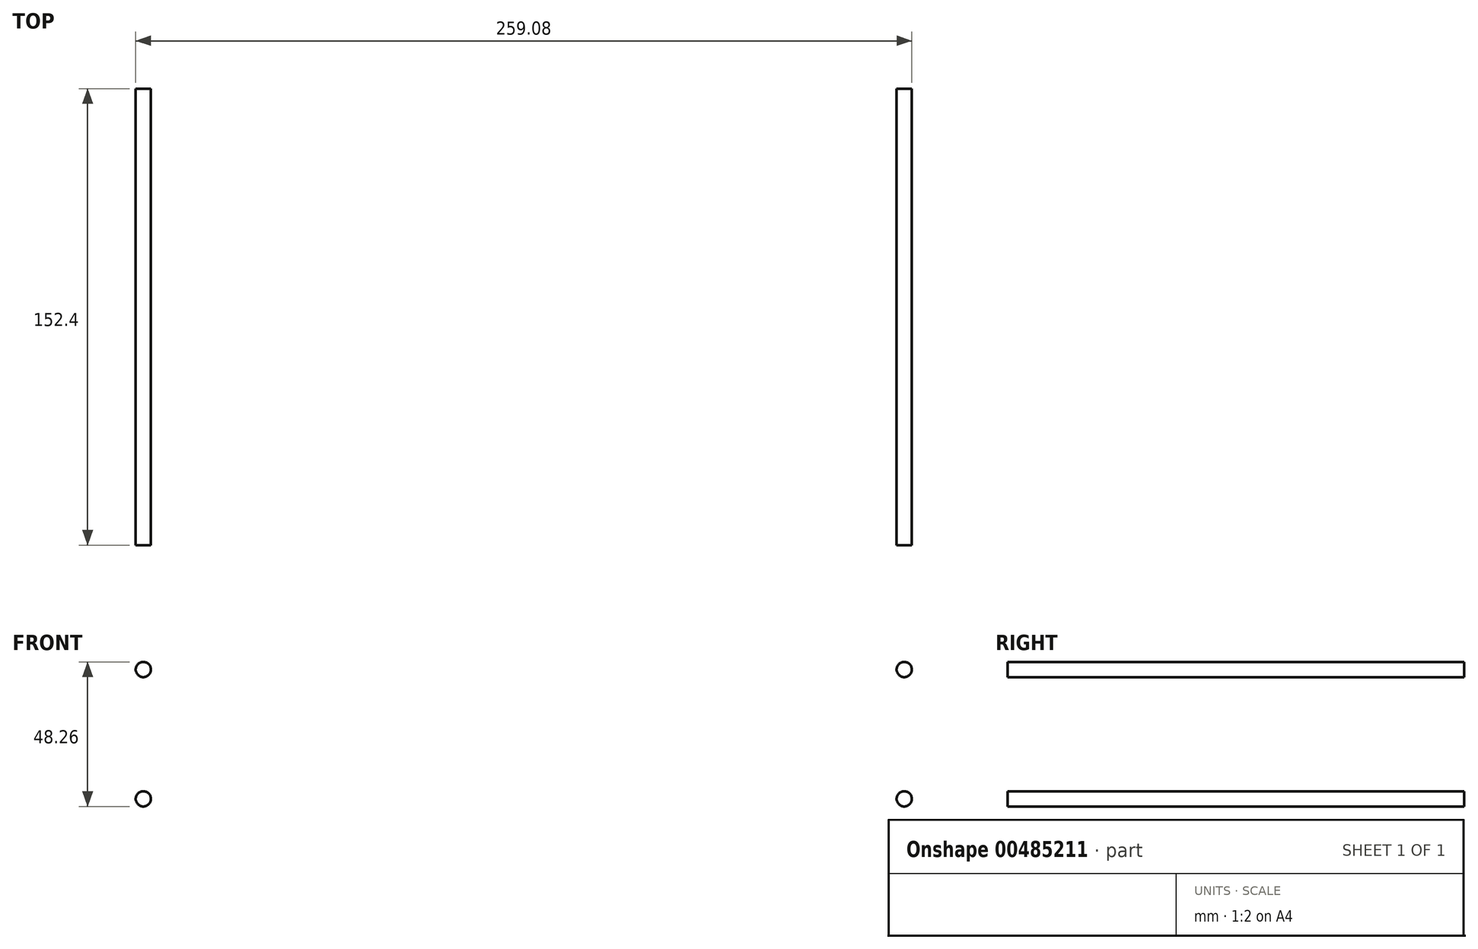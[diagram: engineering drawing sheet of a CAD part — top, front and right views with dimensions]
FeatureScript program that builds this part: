
annotation { "Feature Type Name" : "Feature", "Feature Type Description" : "" }
export const myFeature = defineFeature(function(context is Context, id is Id, definition is map)
    precondition{}
    {
        {
            var Q0;
            Q0=qCreatedBy(makeId("Front.planeOp"),FACE);
            var sketch = newSketch(context, id + "F0", { "sketchPlane" : qUnion([Q0])});
            skCircle(sketch, "E0", {"center": v(-127, 21.59) * mm, "radius": 2.54 * mm});
            skCircle(sketch, "E1", {"center": v(127, 21.59) * mm, "radius": 2.54 * mm});
            skCircle(sketch, "E2", {"center": v(127, -21.59) * mm, "radius": 2.54 * mm});
            skCircle(sketch, "E3", {"center": v(-127, -21.6) * mm, "radius": 2.54 * mm});
            skSolve(sketch);
        }
        {
            var Q0;
            Q0 = qSketchRegion(id + "F0", true);
            extrude(context, id + "F1", {"entities" : qUnion([Q0]), "depth" : 152.4 * mm});
        }
    });
